# Revit family: Metawall® Facade Element
name_source: partatom
category: Generic Models
revit_build: Autodesk Revit 2013 (Build: 20120221_2030(x64)
units: mm (PartAtom-declared; Revit-internal decimal feet)

## types (4) — shared parameters
Bottom Left Cut Panel = No
Bottom Right Cut Panel = No
Date of publishing = 9/11/2012
Design country = Germany
Edition number = 1
Manufacture country = Germany
Manufacturer = Metawell GmbH
Panel Full Panel = Yes
Panel Material = Aluminium
Top Left Cut Panel = No
Top Right Cut Panel = No
URL = http://metawell.bimobject.com
zero-valued in all types: Default Elevation

## per-type parameters (varying)
| type | Product SKU | Product family | Product group |
| H10 Curtain Wall Facade | Matawell_H10_EN_1 | FACADE ENGINEERING | Fasade Elements |
| H10 Vorgehängte hinterlüftete Fassade | Matawell_H10_DE_1 | Bau | Fassadentechnik |
| H15 Curtain Wall Facade | Matawell_H15_EN_1 | FACADE ENGINEERING | Fasade Elements |
| H15 Vorgehängte hinterlüftete Fassade | Matawell_H15_DE_1 | Bau | Fassadentechnik |

note: column(s) folded — value = type name in every type: Model

## geometry (parser evidence)
native form markers: Sweep x1
no freeform markers — native parametric forms only
